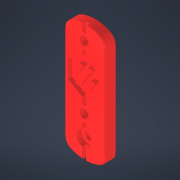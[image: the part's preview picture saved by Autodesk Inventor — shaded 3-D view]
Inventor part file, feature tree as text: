
AUTODESK INVENTOR PART (.ipt)
format: ipt  version: 2022.1 (Build 261234000, 234)  size: 196,096 bytes
history: native  units: mm
features: reference x4, other x3, delete_face x1, hole x1, chamfer x1, sketch x1
ambient origin geometry x8: Origin, YZ Plane, XZ Plane, XY Plane, X Axis, Y Axis, Z Axis, Center Point
bodies: Volumenkörper1 (feature_tree)
feature tree (11):
  delete_face  "Fläche löschen1"
  hole  "Bohrung1"  [1 undecoded]
  chamfer  "Fase1"  [1 undecoded]
  sketch  "Skizze1"  dims[d0=2.4mm d1=6.0mm d2=4.0mm d3=2.0mm d4=90.0deg d5=3.0mm d6=0.0mm d7=0.8mm d8=2.0mm d9=45.0deg]
  reference  "Referenz1"
  reference  "Referenz2"
  reference  "Referenz3"
  reference  "Referenz4"
  other  "[a]_idler_screw_plate"
  other  "Baugruppe1"
  other  "Front-Idlers_Housing:1"
note: 2 required parameter values undecoded (feature->parameter linkage not recoverable at this tier; creation-order binding heuristic only, values carry confidence <= 0.55)
